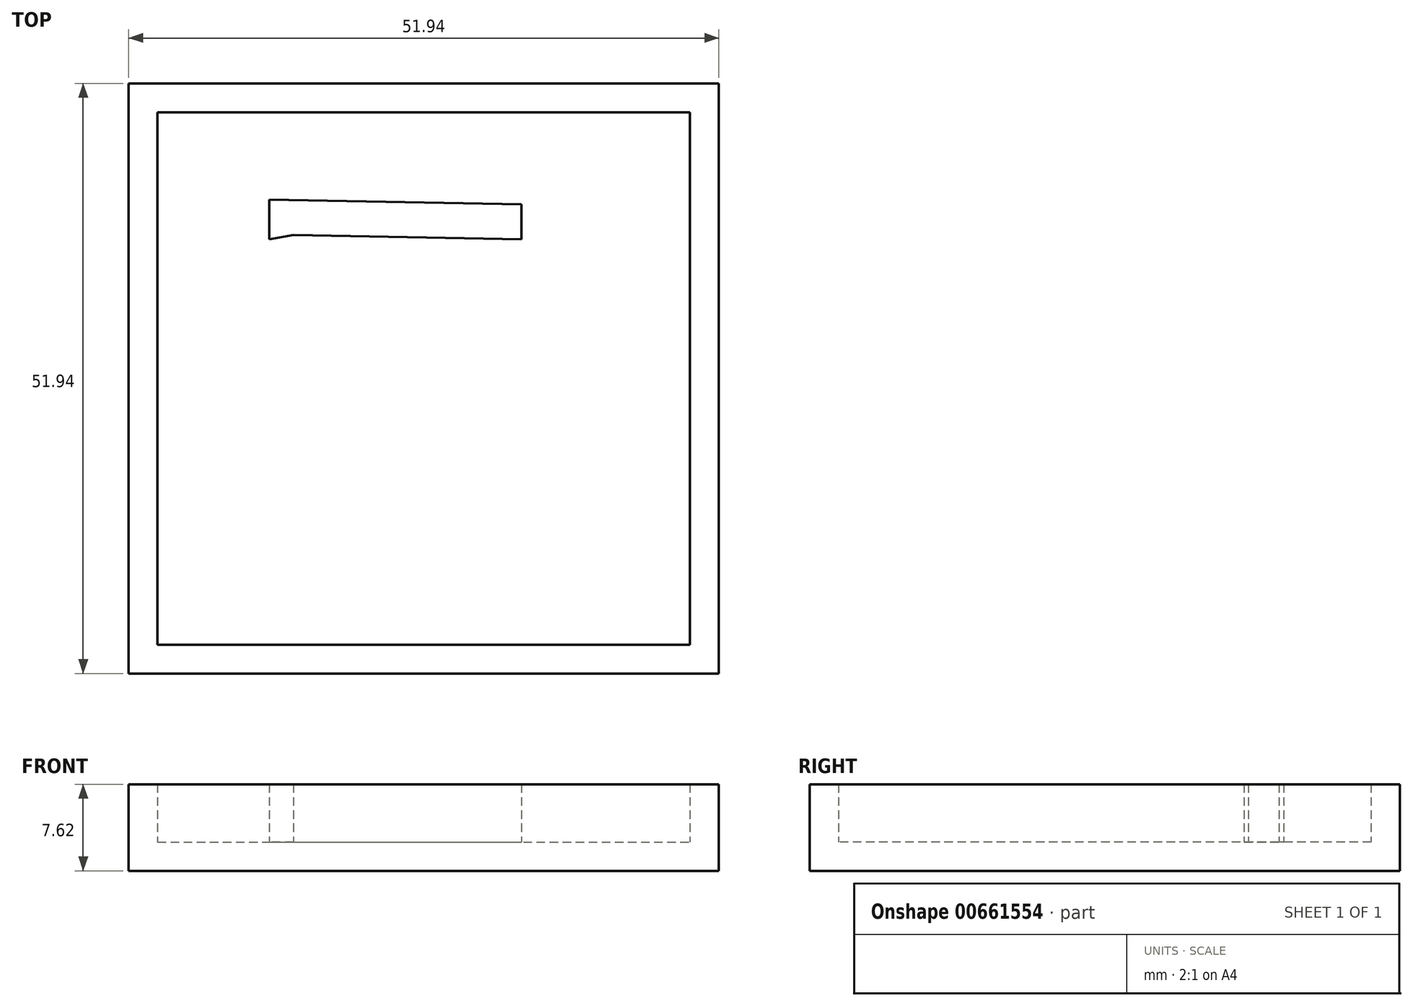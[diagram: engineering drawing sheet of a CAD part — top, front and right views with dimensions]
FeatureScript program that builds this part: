
annotation { "Feature Type Name" : "Feature", "Feature Type Description" : "" }
export const myFeature = defineFeature(function(context is Context, id is Id, definition is map)
    precondition{}
    {
        {
            var Q0;
            Q0=qCreatedBy(makeId("Top.planeOp"),FACE);
            var sketch = newSketch(context, id + "F0", { "sketchPlane" : qUnion([Q0])});
            skLineSegment(sketch, "E0.bottom", {"start": v(0, 0) * mm, "end": v(51.94, 0) * mm});
            skLineSegment(sketch, "E0.top", {"start": v(0, -51.94) * mm, "end": v(51.94, -51.94) * mm});
            skLineSegment(sketch, "E0.left", {"start": v(0, 0) * mm, "end": v(0, -51.94) * mm});
            skLineSegment(sketch, "E0.right", {"start": v(51.94, 0) * mm, "end": v(51.94, -51.94) * mm});
            skSolve(sketch);
        }
        {
            var Q0;
            Q0 = qSketchRegion(id + "F0", true);
            extrude(context, id + "F1", {"entities" : qUnion([Q0]), "depth" : 7.62 * mm, "offsetDistance" : 25.4 * mm});
        }
        {
            var Q0;
            Q0=makeQuery(id+"F1.opExtrude","CAP_FACE",FACE,{"disambiguationData":[OSD([sQuery(id+"F0.wireOp",EDGE,"E0.bottom"),sQuery(id+"F0.wireOp",EDGE,"E0.top"),sQuery(id+"F0.wireOp",EDGE,"E0.left"),sQuery(id+"F0.wireOp",EDGE,"E0.right")])],"isStart":false});
            shell(context, id + "F2", {"entities" : qUnion([Q0]), "thickness" : 2.54 * mm});
        }
        {
            var Q0;
            Q0=makeQuery(id+"F2.opShell","OFFSET_FACE",FACE,{"disambiguationData":[OSD([sQuery(id+"F0.wireOp",EDGE,"E0.bottom"),sQuery(id+"F0.wireOp",EDGE,"E0.top"),sQuery(id+"F0.wireOp",EDGE,"E0.left"),sQuery(id+"F0.wireOp",EDGE,"E0.right")])]});
            var sketch = newSketch(context, id + "F3", { "sketchPlane" : qUnion([Q0])});
            skLineSegment(sketch, "E1", {"start": v(12.36, -49.4) * mm, "end": v(12.36, -13.72) * mm});
            skLineSegment(sketch, "E2", {"start": v(14.5, -49.4) * mm, "end": v(14.5, -13.34) * mm});
            skLineSegment(sketch, "E3", {"start": v(14.5, -13.34) * mm, "end": v(12.36, -13.72) * mm});
            skLineSegment(sketch, "E4", {"start": v(14.5, -13.34) * mm, "end": v(34.55, -13.72) * mm});
            skLineSegment(sketch, "E5", {"start": v(12.36, -13.72) * mm, "end": v(12.36, -10.22) * mm});
            skLineSegment(sketch, "E6", {"start": v(12.36, -10.22) * mm, "end": v(34.55, -10.65) * mm});
            skLineSegment(sketch, "E7", {"start": v(34.55, -10.65) * mm, "end": v(34.55, -13.72) * mm});
            skSolve(sketch);
        }
        {
            var Q0;
            {var subQ0=sQuery(id+"F0.wireOp",EDGE,"E0.bottom");Q0=makeQuery(id+"F3.imprint","IMPRINT",FACE,{"disambiguationData":[TD([[makeQuery(id+"F3.imprint","IMPRINT",EDGE,{"derivedFrom":makeQuery(id+"F2.opShell","OFFSET_EDGE",EDGE,{"disambiguationData":[OSD([subQ0]),TDD([makeQuery(id+"F1.opExtrude","CAP_EDGE",EDGE,{"disambiguationData":[OSD([subQ0])],"isStart":true})])]})}),-1.0]])]});}
            var sketch = newSketch(context, id + "F4", { "sketchPlane" : qUnion([Q0])});
            skSolve(sketch);
        }
        {
            var Q0;
            Q0 = qSketchRegion(id + "F3", true);
            extrude(context, id + "F5", {"entities" : qUnion([Q0]), "operationType" : NewBodyOperationType.ADD, "depth" : 5.08 * mm, "offsetDistance" : 25.4 * mm});
        }
    });
